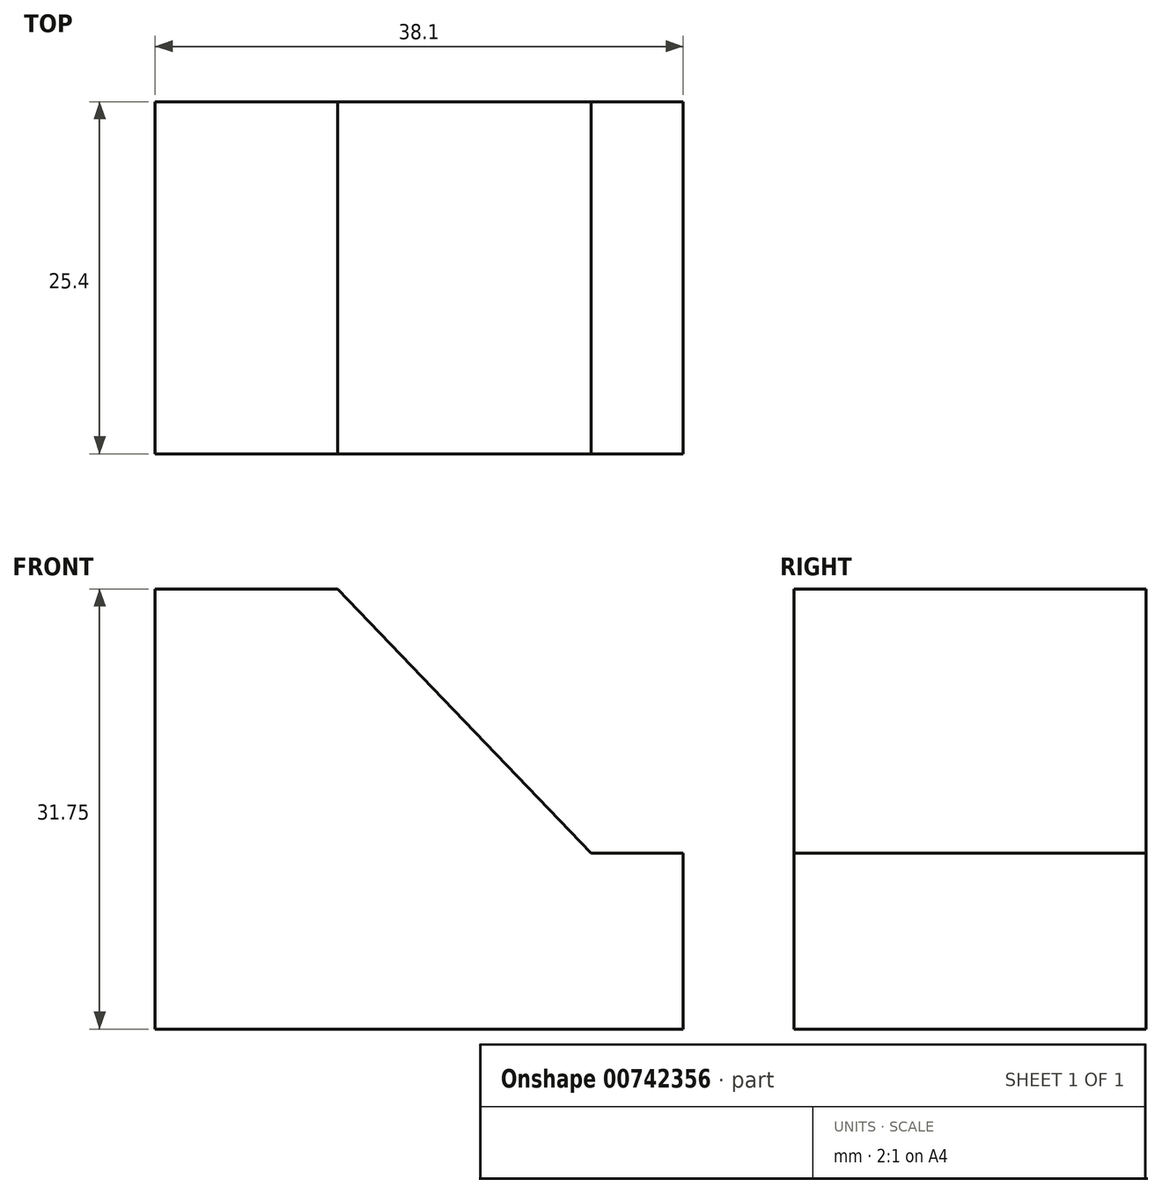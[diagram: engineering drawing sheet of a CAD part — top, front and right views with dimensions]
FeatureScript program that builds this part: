
annotation { "Feature Type Name" : "Feature", "Feature Type Description" : "" }
export const myFeature = defineFeature(function(context is Context, id is Id, definition is map)
    precondition{}
    {
        {
            var Q0;
            Q0=qCreatedBy(makeId("Front.planeOp"),FACE);
            var sketch = newSketch(context, id + "F0", { "sketchPlane" : qUnion([Q0])});
            skLineSegment(sketch, "E0", {"start": v(0, 0) * mm, "end": v(0, 31.75) * mm});
            skLineSegment(sketch, "E1", {"start": v(0, 31.75) * mm, "end": v(38.1, 31.75) * mm});
            skLineSegment(sketch, "E2", {"start": v(38.1, 31.75) * mm, "end": v(38.1, 0) * mm});
            skLineSegment(sketch, "E3", {"start": v(0, 0) * mm, "end": v(38.1, 0) * mm});
            skSolve(sketch);
        }
        {
            var Q0;
            Q0 = qSketchRegion(id + "F0", true);
            extrude(context, id + "F1", {"entities" : qUnion([Q0]), "depth" : 25.4 * mm, "offsetDistance" : 25.4 * mm});
        }
        {
            var Q0;
            Q0=makeQuery(id+"F1.opExtrude","CAP_FACE",FACE,{"disambiguationData":[OSD([sQuery(id+"F0.wireOp",EDGE,"E0"),sQuery(id+"F0.wireOp",EDGE,"E1"),sQuery(id+"F0.wireOp",EDGE,"E2"),sQuery(id+"F0.wireOp",EDGE,"E3")])],"isStart":true});
            var sketch = newSketch(context, id + "F2", { "sketchPlane" : qUnion([Q0])});
            skLineSegment(sketch, "E4", {"start": v(-13.17, 31.75) * mm, "end": v(-31.45, 12.7) * mm});
            skLineSegment(sketch, "E5", {"start": v(-31.45, 12.7) * mm, "end": v(-38.1, 12.7) * mm});
            skSolve(sketch);
        }
        {
            var Q0;
            Q0 = qSketchRegion(id + "F2", true);
            var Q1;
            {var subQ0=sQuery(id+"F2.wireOp",EDGE,"E4");Q1=makeQuery(id+"F2.imprint","IMPRINT",FACE,{"disambiguationData":[TD([[makeQuery(id+"F2.imprint","IMPRINT",EDGE,{"derivedFrom":subQ0}),-1.0]])]});}
            extrude(context, id + "F3", {"entities" : qUnion([Q0, Q1]), "operationType" : NewBodyOperationType.REMOVE, "endBound" : BoundingType.THROUGH_ALL, "oppositeDirection" : true, "depth" : 25.4 * mm, "offsetDistance" : 25.4 * mm});
        }
    });
